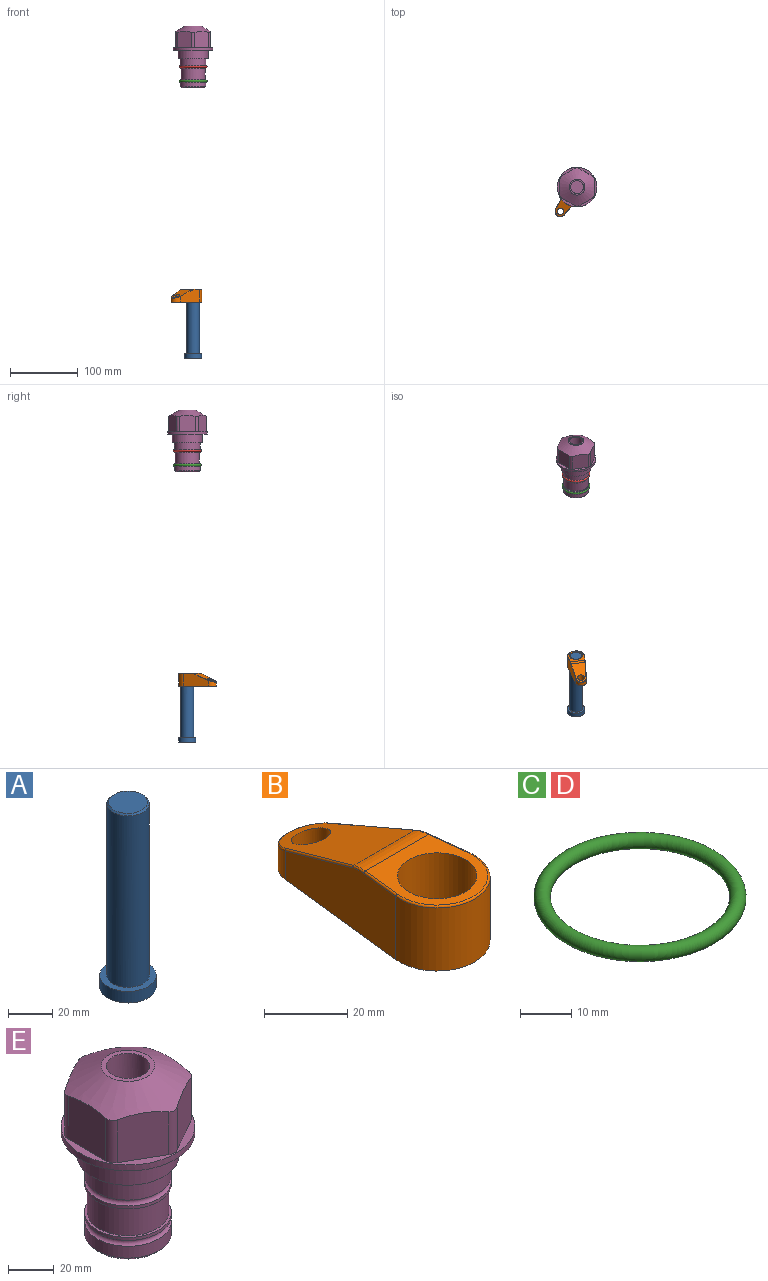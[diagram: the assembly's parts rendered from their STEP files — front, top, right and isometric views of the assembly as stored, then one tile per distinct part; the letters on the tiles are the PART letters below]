
ASSEMBLY  parts=5 mates=3
PART A: 6 faces, bbox 25.4x25.4x101.6 mm
  f0: plane 17.46x17.46mm, normal (0,0,1), area 239.5mm2, adj f5
  f1: plane 25.4x25.4mm, normal (0,0,-1), area 506.7mm2, adj f2
  f2: cylinder r=12.7mm len=25.4mm, axis (0,0,1), area 506.7mm2, adj f1,f3
  f3: plane 25.4x25.4mm, normal (0,0,1), area 221.7mm2, adj f2,f4
  f4: cylinder r=9.53mm len=94.46mm, axis (0,0,1), area 5653mm2, adj f3,f5
  f5: cone r=8.73mm half-angle=45deg, axis (0,0,-1), area 64.4mm2, adj f0,f4
PART B: 44 faces, bbox 27.5x64.5x19.1 mm
  f0: plane 2.3x0.95mm, normal (0,0,-1), area 1mm2, adj f25,f30,f34
  f1: plane 63.5x25.4mm, normal (0,0,-1), area 561.7mm2, adj f2,f3,f4,f5,f6,f7,f19,f20
  f2: cylinder r=12.7mm len=25.4mm, axis (0,0,-1), area 792.2mm2, adj f1,f3,f5,f13
  f3: plane 42.33x18.54mm, normal (0.99,0.11,0), area 647mm2, adj f1,f2,f4,f11,f12,f14
  f4: cylinder r=7.94mm len=15.78mm, axis (0,0,-1), area 158.6mm2, adj f1,f3,f5,f16
  f5: plane 42.33x18.54mm, normal (-0.99,0.11,0), area 647mm2, adj f1,f2,f4,f15,f17,f18
  f6: cylinder r=9.53mm len=19.05mm, axis (0,0,-1), area 1140.1mm2, adj f1,f8
  f7: cylinder r=4.76mm len=10.98mm, axis (0,0,-1), area 276.1mm2, adj f1,f9
  f8: plane 25.83x24.38mm, normal (0,0,1), area 262.2mm2, adj f6,f10,f11,f13,f15
  f9: plane 32.49x20.55mm, normal (0,0.34,0.94), area 489.9mm2, adj f7,f10,f14,f16,f18
  f10: cylinder r=12.7mm len=21.49mm, axis (-1,0,0), area 93.2mm2, adj f8,f9,f12,f17
  f11: cylinder r=0.51mm len=12.34mm, axis (0.11,-0.99,0), area 9.9mm2, adj f3,f8,f12,f13
  f12: bspline ~7.62x1.64mm, area 3.5mm2, adj f3,f10,f11,f14
  f13: torus R=12.19mm, axis (0,0,1), area 33.6mm2, adj f2,f8,f11,f15
  f14: cylinder r=0.51mm len=26.01mm, axis (0.1,-0.93,0.34), area 21.6mm2, adj f3,f9,f12,f16
  f15: cylinder r=0.51mm len=12.34mm, axis (0.11,0.99,0), area 9.9mm2, adj f5,f8,f13,f17
  f16: bspline ~15.78x7.05mm, area 15.7mm2, adj f4,f9,f14,f18
  f17: bspline ~7.62x1.64mm, area 3.5mm2, adj f5,f10,f15,f18
  f18: cylinder r=0.51mm len=26.01mm, axis (0.1,0.93,-0.34), area 21.6mm2, adj f5,f9,f16,f17
  f19: plane 21.6x14.29mm, normal (-0.99,-0.11,0), area 242.6mm2, adj f1,f26,f28,f34,f36,f38
  f20: plane 21.6x14.29mm, normal (0.99,-0.11,0), area 242.6mm2, adj f1,f27,f29,f37,f39,f41
  f21: cylinder r=12.7mm len=14.29mm, axis (0,0,-1), area 173.2mm2, adj f1,f26,f27,f30,f31,f33
  f22: cylinder r=7.94mm len=7.63mm, axis (0,0,-1), area 53.8mm2, adj f1,f28,f29,f42
  f23: plane 2.3x0.95mm, normal (0,0,-1), area 1mm2, adj f25,f33,f37
  f24: plane 17.94x12.32mm, normal (0,-0.34,-0.94), area 191.2mm2, adj f25,f38,f41,f42
  f25: cylinder r=9.53mm len=12.93mm, axis (-1,0,0), area 37.5mm2, adj f0,f23,f24,f31,f36,f39
  f26: cylinder r=1.59mm len=14.29mm, axis (0,0,-1), area 49mm2, adj f1,f19,f21,f32
  f27: cylinder r=1.59mm len=14.29mm, axis (0,0,-1), area 49mm2, adj f1,f20,f21,f35
  f28: cylinder r=1.59mm len=7.28mm, axis (0,0,-1), area 22.1mm2, adj f1,f19,f22,f40
  f29: cylinder r=1.59mm len=7.28mm, axis (0,0,-1), area 22.1mm2, adj f1,f20,f22,f43
  f30: torus R=14.29mm, axis (0,0,1), area 5.8mm2, adj f0,f21,f31,f32
  f31: bspline ~11.06x2.73mm, area 20.8mm2, adj f21,f25,f30,f33
  f32: sphere r=1.59mm, area 5.4mm2, adj f26,f30,f34
  f33: torus R=14.29mm, axis (0,0,1), area 5.8mm2, adj f21,f23,f31,f35
  f34: cylinder r=1.59mm len=1.68mm, axis (-0.11,0.99,0), area 2.4mm2, adj f0,f19,f32,f36
  f35: sphere r=1.59mm, area 5.4mm2, adj f27,f33,f37
  f36: bspline ~5.82x2.33mm, area 7.7mm2, adj f19,f25,f34,f38
  f37: cylinder r=1.59mm len=1.68mm, axis (0.11,0.99,0), area 2.4mm2, adj f20,f23,f35,f39
  f38: cylinder r=1.59mm len=18.33mm, axis (0.1,-0.93,0.34), area 46.7mm2, adj f19,f24,f36,f40
  f39: bspline ~5.82x2.33mm, area 7.7mm2, adj f20,f25,f37,f41
  f40: sphere r=1.59mm, area 3.6mm2, adj f28,f38,f42
  f41: cylinder r=1.59mm len=18.33mm, axis (0.1,0.93,-0.34), area 46.7mm2, adj f20,f24,f39,f43
  f42: bspline ~8.31x1.84mm, area 15.3mm2, adj f22,f24,f40,f43
  f43: sphere r=1.59mm, area 3.6mm2, adj f29,f41,f42
PART C: 1 faces, bbox 44.7x44.7x3.2 mm
  f0: torus R=19.05mm, axis (0,0,1), area 1193.9mm2
PART D: same geometry as C
PART E: 36 faces, bbox 58.7x58.7x91.2 mm
  f0: cylinder r=17.78mm len=35.56mm, axis (0,0,1), area 1670.8mm2, adj f23,f24,f31
  f1: cylinder r=19.05mm len=38.1mm, axis (0,0,1), area 1191.9mm2, adj f26,f27,f30
  f2: plane 58.66x58.66mm, normal (0,0,-1), area 1150.6mm2, adj f3,f28
  f3: cylinder r=29.33mm len=58.66mm, axis (0,0,-1), area 585.1mm2, adj f2,f4
  f4: plane 58.66x58.66mm, normal (0,0,1), area 475.9mm2, adj f3,f5,f6,f7,f8,f9,f10,f11
  f5: plane 24.5x20.32mm, normal (-0.5,0.87,0), area 562.8mm2, adj f4,f15,f16,f17
  f6: plane 24.5x20.32mm, normal (0.5,0.87,0), area 562.8mm2, adj f4,f14,f15,f17
  f7: plane 24.5x23.48mm, normal (1,0,0), area 562.8mm2, adj f4,f13,f14,f17
  f8: plane 24.5x20.32mm, normal (0.5,-0.87,0), area 562.8mm2, adj f4,f12,f13,f17
  f9: plane 24.5x20.32mm, normal (-0.5,-0.87,0), area 562.8mm2, adj f4,f11,f12,f17
  f10: plane 24.5x23.48mm, normal (-1,0,0), area 562.8mm2, adj f4,f11,f16,f17
  f11: cylinder r=5.08mm len=23.01mm, axis (0,0,-1), area 121.2mm2, adj f4,f9,f10,f17
  f12: cylinder r=5.08mm len=23.01mm, axis (0,0,-1), area 121.2mm2, adj f4,f8,f9,f17
  f13: cylinder r=5.08mm len=23.01mm, axis (0,0,-1), area 121.2mm2, adj f4,f7,f8,f17
  f14: cylinder r=5.08mm len=23.01mm, axis (0,0,-1), area 121.2mm2, adj f4,f6,f7,f17
  f15: cylinder r=5.08mm len=23.01mm, axis (0,0,-1), area 121.2mm2, adj f4,f5,f6,f17
  f16: cylinder r=5.08mm len=23.01mm, axis (0,0,-1), area 121.2mm2, adj f4,f5,f10,f17
  f17: cone r=11.73mm half-angle=60deg, axis (0,0,-1), area 2071.8mm2, adj f5,f6,f7,f8,f9,f10,f11,f12
  f18: plane 23.46x23.46mm, normal (0,0,1), area 147.4mm2, adj f17,f35
  f19: plane 34.93x34.93mm, normal (0,0,-1), area 958mm2, adj f29
  f20: cylinder r=19.05mm len=38.1mm, axis (0,0,1), area 760.1mm2, adj f21,f29
  f21: torus R=19.05mm, axis (0,0,1), area 565.3mm2, adj f20,f22
  f22: cylinder r=19.05mm len=38.1mm, axis (0,0,1), area 190mm2, adj f21,f23
  f23: plane 38.1x38.1mm, normal (0,0,1), area 146.9mm2, adj f0,f22
  f24: plane 38.1x38.1mm, normal (0,0,-1), area 146.9mm2, adj f0,f25
  f25: cylinder r=19.05mm len=38.1mm, axis (0,0,1), area 190mm2, adj f24,f26
  f26: torus R=19.05mm, axis (0,0,1), area 565.3mm2, adj f1,f25
  f27: plane 44.45x44.45mm, normal (0,0,-1), area 411.7mm2, adj f1,f28
  f28: cylinder r=22.23mm len=44.45mm, axis (0,0,1), area 1773.5mm2, adj f2,f27
  f29: cone r=19.05mm half-angle=45deg, axis (0,0,1), area 257.5mm2, adj f19,f20
  f30: cylinder r=3.17mm len=6.75mm, axis (-1,0,0), area 128mm2, adj f1,f33
  f31: cylinder r=3.17mm len=6.35mm, axis (-1,0,0), area 102.5mm2, adj f0,f33
  f32: plane 25.4x25.4mm, normal (0,0,1), area 506.7mm2, adj f33
  f33: cylinder r=12.7mm len=66.42mm, axis (0,0,-1), area 5236.2mm2, adj f30,f31,f32,f34
  f34: cone r=9.53mm half-angle=30deg, axis (0,0,-1), area 443.4mm2, adj f33,f35
  f35: cylinder r=9.53mm len=19.05mm, axis (0,0,-1), area 849mm2, adj f18,f34
PLACE A rot(axis=(0,0,-1),125deg) t=(0,0,-427.46)mm
PLACE B rot(axis=(0,0,1),145deg) t=(0,0,-372.85)mm
PLACE C t=(0,0,-21.59)mm
PLACE D at identity
PLACE E at identity fixed
MATE fastened C.f0 <-> E.f0  axis (0,0,1) through (0,0,-46.1)mm
MATE cylindrical A.f2 <-> E.f0  axis (0,0,1) through (0,0,-401.82)mm
MATE fastened B.f2 <-> A.f2  axis (0,0,1) through (0,0,-353.8)mm
